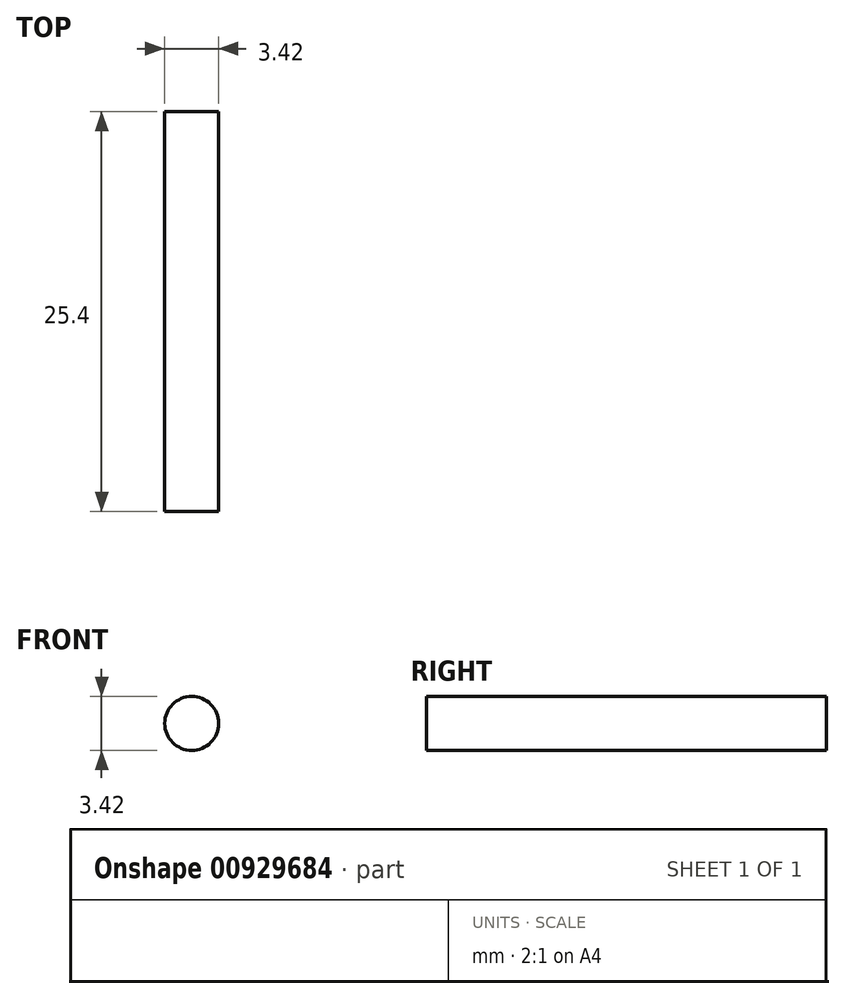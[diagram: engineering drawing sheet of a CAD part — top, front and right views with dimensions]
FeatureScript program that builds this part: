
annotation { "Feature Type Name" : "Feature", "Feature Type Description" : "" }
export const myFeature = defineFeature(function(context is Context, id is Id, definition is map)
    precondition{}
    {
        {
            var Q0;
            Q0=qCreatedBy(makeId("Front.planeOp"),FACE);
            var sketch = newSketch(context, id + "F0", { "sketchPlane" : qUnion([Q0])});
            skCircle(sketch, "E0", {"center": v(0, 0) * mm, "radius": 1.71 * mm});
            skSolve(sketch);
        }
        {
            var Q0;
            Q0=qSketchRegion(id+"F0",true);
            extrude(context, id + "F1", {"entities" : qUnion([Q0]), "depth" : 25.4 * mm, "offsetDistance" : 25.4 * mm});
        }
    });
